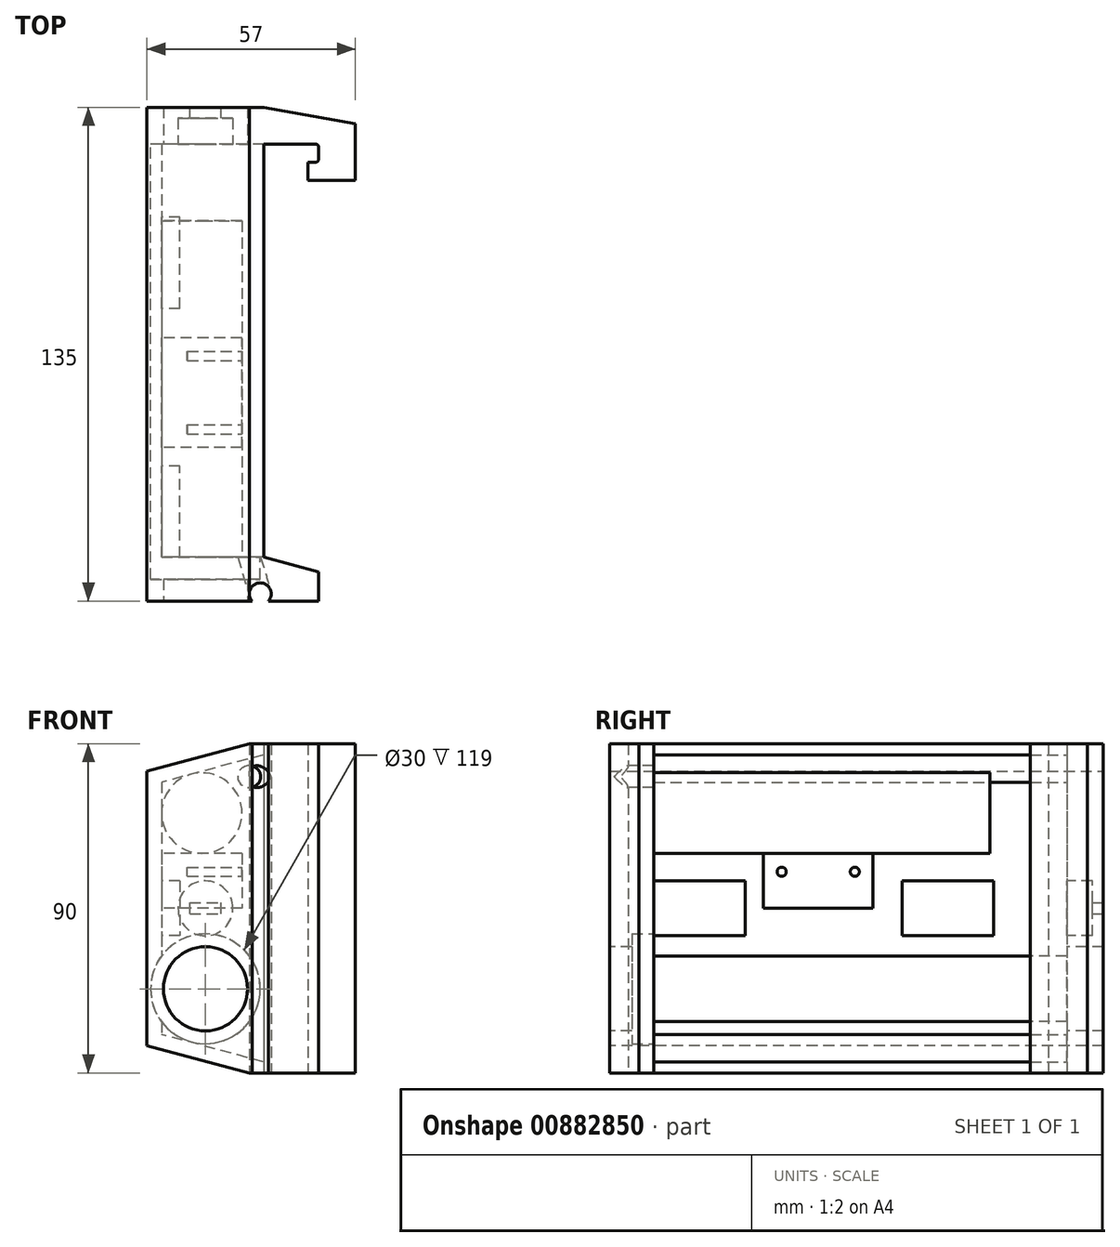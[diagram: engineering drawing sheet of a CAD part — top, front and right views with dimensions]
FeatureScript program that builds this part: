
annotation { "Feature Type Name" : "Feature", "Feature Type Description" : "" }
export const myFeature = defineFeature(function(context is Context, id is Id, definition is map)
    precondition{}
    {
        {
            var Q0;
            Q0=qCreatedBy(makeId("Top.planeOp"),FACE);
            var sketch = newSketch(context, id + "F0", { "sketchPlane" : qUnion([Q0])});
            skLineSegment(sketch, "E0", {"start": v(0, 0) * mm, "end": v(15, 0) * mm});
            skLineSegment(sketch, "E1", {"start": v(15, 0) * mm, "end": v(15, -5) * mm});
            skLineSegment(sketch, "E2", {"start": v(15, -5) * mm, "end": v(12, -5) * mm});
            skLineSegment(sketch, "E3", {"start": v(12, -5) * mm, "end": v(12, -10) * mm});
            skLineSegment(sketch, "E4", {"start": v(12, -10) * mm, "end": v(25, -10) * mm});
            skLineSegment(sketch, "E5", {"start": v(25, -10) * mm, "end": v(25, 10) * mm});
            skLineSegment(sketch, "E6", {"start": v(25, 10) * mm, "end": v(-32, 10) * mm});
            skLineSegment(sketch, "E7", {"start": v(-32, 10) * mm, "end": v(-32, -125) * mm});
            skLineSegment(sketch, "E8", {"start": v(15, -117.02) * mm, "end": v(0, -113) * mm});
            skLineSegment(sketch, "E9", {"start": v(0, -113) * mm, "end": v(0, 0) * mm});
            skLineSegment(sketch, "E10", {"start": v(-32, -125) * mm, "end": v(-3.24, -125) * mm});
            skLineSegment(sketch, "E11", {"start": v(15, -125) * mm, "end": v(15, -117.02) * mm});
            skArc(sketch, "E12", {"start": v(1.24, -125) * mm, "mid": v(-1, -120) * mm, "end": v(-3.24, -125) * mm});
            skLineSegment(sketch, "E13.trimOffspring", {"start": v(1.24, -125) * mm, "end": v(15, -125) * mm});
            skSolve(sketch);
        }
        {
            var Q0;
            Q0=qSketchRegion(id+"F0",true);
            extrude(context, id + "F1", {"entities" : qUnion([Q0]), "depth" : 90 * mm, "symmetric" : true});
        }
        {
            var Q0;
            Q0=makeQuery(id+"F1.opExtrude","CAP_EDGE",EDGE,{"disambiguationData":[OSD([sQuery(id+"F0.wireOp",EDGE,"E7")])],"isStart":false});
            chamfer(context, id + "F2", {"entities" : qUnion([Q0]), "chamferType" : ChamferType.OFFSET_ANGLE, "width" : 28 * mm, "oppositeDirection" : false, "angle" : 15 * degree, "tangentPropagation" : true});
        }
        {
            var Q0;
            Q0=makeQuery(id+"F1.opExtrude","CAP_EDGE",EDGE,{"disambiguationData":[OSD([sQuery(id+"F0.wireOp",EDGE,"E7")])],"isStart":true});
            chamfer(context, id + "F3", {"entities" : qUnion([Q0]), "chamferType" : ChamferType.OFFSET_ANGLE, "width" : 28 * mm, "oppositeDirection" : true, "angle" : 15 * degree, "tangentPropagation" : true});
        }
        {
            var Q0;
            Q0=makeQuery(id+"F1.opExtrude","SWEPT_FACE",FACE,{"disambiguationData":[OSD([sQuery(id+"F0.wireOp",EDGE,"E0")])]});
            var sketch = newSketch(context, id + "F4", { "sketchPlane" : qUnion([Q0])});
            skLineSegment(sketch, "E14", {"start": v(0, 0) * mm, "end": v(0, -42) * mm});
            skLineSegment(sketch, "E15", {"start": v(0, -42) * mm, "end": v(-28, -34.5) * mm});
            skLineSegment(sketch, "E16", {"start": v(-28, -34.5) * mm, "end": v(-28, 0) * mm});
            skLineSegment(sketch, "E17", {"start": v(-28, 0) * mm, "end": v(0, 0) * mm, "construction": true});
            skLineSegment(sketch, "E18.MirrorCS", {"start": v(0, 42) * mm, "end": v(-28, 34.5) * mm});
            skLineSegment(sketch, "E19.MirrorCS", {"start": v(0, 0) * mm, "end": v(0, 42) * mm});
            skLineSegment(sketch, "E20.MirrorCS", {"start": v(-28, 34.5) * mm, "end": v(-28, 0) * mm});
            skSolve(sketch);
        }
        {
            var Q0;
            Q0 = qSketchRegion(id + "F4", true);
            extrude(context, id + "F5", {"entities" : qUnion([Q0]), "operationType" : NewBodyOperationType.REMOVE, "depth" : 113 * mm, "offsetDistance" : 25 * mm});
        }
        {
            var Q0;
            Q0=makeQuery(id+"F1.opExtrude","SWEPT_FACE",FACE,{"disambiguationData":[OSD([sQuery(id+"F0.wireOp",EDGE,"E10")])]});
            var sketch = newSketch(context, id + "F6", { "sketchPlane" : qUnion([Q0])});
            skCircle(sketch, "E21", {"center": v(-16, -22) * mm, "radius": 11.5 * mm});
            skSolve(sketch);
        }
        {
            var Q0;
            Q0 = qSketchRegion(id + "F6", true);
            extrude(context, id + "F7", {"entities" : qUnion([Q0]), "operationType" : NewBodyOperationType.REMOVE, "endBound" : BoundingType.THROUGH_ALL, "oppositeDirection" : true, "depth" : 25 * mm, "offsetDistance" : 25 * mm});
        }
        {
            var Q0;
            Q0=makeQuery(id+"F5.boolean.opBoolean","COPY",FACE,{"derivedFrom":makeQuery(id+"F5.opExtrude","CAP_FACE",FACE,{"disambiguationData":[OSD([sQuery(id+"F4.wireOp",EDGE,"E14"),sQuery(id+"F4.wireOp",EDGE,"E15"),sQuery(id+"F4.wireOp",EDGE,"E16"),sQuery(id+"F4.wireOp",EDGE,"E19.MirrorCS"),sQuery(id+"F4.wireOp",EDGE,"E18.MirrorCS"),sQuery(id+"F4.wireOp",EDGE,"E20.MirrorCS")])],"isStart":false})});
            var sketch = newSketch(context, id + "F8", { "sketchPlane" : qUnion([Q0])});
            skCircle(sketch, "E22", {"center": v(16, -22) * mm, "radius": 15 * mm});
            skSolve(sketch);
        }
        {
            var Q0;
            Q0 = qSketchRegion(id + "F8", true);
            extrude(context, id + "F9", {"entities" : qUnion([Q0]), "operationType" : NewBodyOperationType.REMOVE, "oppositeDirection" : true, "depth" : 6 * mm, "offsetDistance" : 25 * mm});
        }
        {
            var Q0;
            Q0 = qSketchRegion(id + "F8", true);
            var Q1;
            Q1=makeQuery(id+"FtUT5HdTIuJWpzB_1.boolean.opBoolean","MERGE",FACE,{"derivedFrom":[makeQuery(id+"F1.opExtrude","SWEPT_FACE",FACE,{"disambiguationData":[OSD([sQuery(id+"F0.wireOp",EDGE,"E0")])]})],"fromTools":[makeQuery(id+"FtUT5HdTIuJWpzB_1.opExtrude","SWEPT_FACE",FACE,{"disambiguationData":[OSD([sQuery(id+"FxggytiENuwNWFf_1.wireOp",EDGE,"w0qHnqGK-W6aV-OTm7-zip8-LkYYj01r2KTm.left")])]})]});
            extrude(context, id + "F10", {"entities" : qUnion([Q0]), "operationType" : NewBodyOperationType.REMOVE, "endBound" : BoundingType.UP_TO_SURFACE, "depth" : 60 * mm, "endBoundEntityFace" : qUnion([Q1]), "offsetDistance" : 25 * mm});
        }
        {
            var Q0;
            {var subQ1=sQuery(id+"F4.wireOp",EDGE,"E20.MirrorCS");var subQ2=sQuery(id+"F4.wireOp",EDGE,"E18.MirrorCS");var subQ3=sQuery(id+"F4.wireOp",EDGE,"E16");Q0=makeQuery(id+"F10.boolean.opBoolean","SPLIT",FACE,{"disambiguationData":[TD([makeQuery(id+"F5.boolean.opBoolean","COPY",FACE,{"derivedFrom":makeQuery(id+"F5.opExtrude","SWEPT_FACE",FACE,{"disambiguationData":[OSD([subQ2])]})})])],"derivedFrom":makeQuery(id+"F5.boolean.opBoolean","COPY",FACE,{"derivedFrom":makeQuery(id+"F5.opExtrude","SWEPT_FACE",FACE,{"disambiguationData":[OSD([subQ3,subQ1])]})})});}
            var sketch = newSketch(context, id + "F11", { "sketchPlane" : qUnion([Q0])});
            skLineSegment(sketch, "E23.bottom", {"start": v(-83, 15) * mm, "end": v(-53, 15) * mm});
            skLineSegment(sketch, "E23.top", {"start": v(-83, 0) * mm, "end": v(-53, 0) * mm});
            skLineSegment(sketch, "E23.left", {"start": v(-83, 15) * mm, "end": v(-83, 0) * mm});
            skLineSegment(sketch, "E23.right", {"start": v(-53, 15) * mm, "end": v(-53, 0) * mm});
            skSolve(sketch);
        }
        {
            var Q0;
            Q0 = qSketchRegion(id + "F11", true);
            extrude(context, id + "F12", {"entities" : qUnion([Q0]), "operationType" : NewBodyOperationType.ADD, "depth" : 22 * mm, "offsetDistance" : 25 * mm});
        }
        {
            var Q0;
            Q0=makeQuery(id+"F12.opExtrude","CAP_FACE",FACE,{"disambiguationData":[OSD([sQuery(id+"F11.wireOp",EDGE,"E23.bottom"),sQuery(id+"F11.wireOp",EDGE,"E23.top"),sQuery(id+"F11.wireOp",EDGE,"E23.left"),sQuery(id+"F11.wireOp",EDGE,"E23.right")])],"isStart":false});
            var sketch = newSketch(context, id + "F13", { "sketchPlane" : qUnion([Q0])});
            skCircle(sketch, "E24", {"center": v(-78, 10) * mm, "radius": 1.25 * mm});
            skCircle(sketch, "E25", {"center": v(-58, 10) * mm, "radius": 1.25 * mm});
            skLineSegment(sketch, "E26", {"start": v(-78, 10) * mm, "end": v(-58, 10) * mm, "construction": true});
            skLineSegment(sketch, "E27", {"start": v(-68, 10) * mm, "end": v(-68, 15) * mm, "construction": true});
            skSolve(sketch);
        }
        {
            var Q0;
            Q0 = qSketchRegion(id + "F13", true);
            extrude(context, id + "F14", {"entities" : qUnion([Q0]), "operationType" : NewBodyOperationType.REMOVE, "oppositeDirection" : true, "depth" : 15 * mm, "offsetDistance" : 25 * mm});
        }
        {
            var Q0;
            Q0=makeQuery(id+"F1.opExtrude","SWEPT_FACE",FACE,{"disambiguationData":[OSD([sQuery(id+"F0.wireOp",EDGE,"E6")])]});
            var sketch = newSketch(context, id + "F15", { "sketchPlane" : qUnion([Q0])});
            skLineSegment(sketch, "E28.bottom", {"start": v(20.25, -1.5) * mm, "end": v(11.75, -1.5) * mm});
            skLineSegment(sketch, "E28.top", {"start": v(20.25, 1.5) * mm, "end": v(11.75, 1.5) * mm});
            skLineSegment(sketch, "E28.left", {"start": v(20.25, -1.5) * mm, "end": v(20.25, 1.5) * mm});
            skLineSegment(sketch, "E28.right", {"start": v(11.75, -1.5) * mm, "end": v(11.75, 1.5) * mm});
            skLineSegment(sketch, "E29", {"start": v(16, -22) * mm, "end": v(16, -1.5) * mm, "construction": true});
            skLineSegment(sketch, "E30", {"start": v(11.75, 0) * mm, "end": v(0, 0) * mm, "construction": true});
            skSolve(sketch);
        }
        {
            var Q0;
            Q0 = qSketchRegion(id + "F15", true);
            extrude(context, id + "F16", {"entities" : qUnion([Q0]), "operationType" : NewBodyOperationType.REMOVE, "endBound" : BoundingType.UP_TO_NEXT, "oppositeDirection" : true, "depth" : 25 * mm, "offsetDistance" : 25 * mm});
        }
        {
            var Q0;
            Q0=makeQuery(id+"F10.boolean.opBoolean","MERGE",FACE,{"derivedFrom":[makeQuery(id+"F5.boolean.opBoolean","MERGE",FACE,{"derivedFrom":[makeQuery(id+"F1.opExtrude","SWEPT_FACE",FACE,{"disambiguationData":[OSD([sQuery(id+"F0.wireOp",EDGE,"E0")])]})],"fromTools":[makeQuery(id+"F5.opExtrude","CAP_FACE",FACE,{"disambiguationData":[OSD([sQuery(id+"F4.wireOp",EDGE,"E14"),sQuery(id+"F4.wireOp",EDGE,"E15"),sQuery(id+"F4.wireOp",EDGE,"E16"),sQuery(id+"F4.wireOp",EDGE,"E19.MirrorCS"),sQuery(id+"F4.wireOp",EDGE,"E18.MirrorCS"),sQuery(id+"F4.wireOp",EDGE,"E20.MirrorCS")])],"isStart":true})]})],"fromTools":[makeQuery(id+"F10.opExtrude","CAP_FACE",FACE,{"disambiguationData":[OSD([sQuery(id+"F8.wireOp",EDGE,"E22")])],"isStart":false})]});
            var sketch = newSketch(context, id + "F17", { "sketchPlane" : qUnion([Q0])});
            skLineSegment(sketch, "E31", {"start": v(-20.25, 1.5) * mm, "end": v(-11.75, -1.5) * mm, "construction": true});
            skCircle(sketch, "E32", {"center": v(-16, 0) * mm, "radius": 7.5 * mm});
            skSolve(sketch);
        }
        {
            var Q0;
            Q0 = qSketchRegion(id + "F17", true);
            extrude(context, id + "F18", {"entities" : qUnion([Q0]), "operationType" : NewBodyOperationType.REMOVE, "oppositeDirection" : true, "depth" : 7 * mm, "offsetDistance" : 25 * mm});
        }
        {
            var Q0;
            {var subQ1=sQuery(id+"F4.wireOp",EDGE,"E20.MirrorCS");var subQ2=sQuery(id+"F4.wireOp",EDGE,"E18.MirrorCS");var subQ3=sQuery(id+"F4.wireOp",EDGE,"E16");Q0=makeQuery(id+"F10.boolean.opBoolean","SPLIT",FACE,{"disambiguationData":[TD([makeQuery(id+"F5.boolean.opBoolean","COPY",FACE,{"derivedFrom":makeQuery(id+"F5.opExtrude","SWEPT_FACE",FACE,{"disambiguationData":[OSD([subQ2])]})})])],"derivedFrom":makeQuery(id+"F5.boolean.opBoolean","COPY",FACE,{"derivedFrom":makeQuery(id+"F5.opExtrude","SWEPT_FACE",FACE,{"disambiguationData":[OSD([subQ3,subQ1])]})})});}
            var sketch = newSketch(context, id + "F19", { "sketchPlane" : qUnion([Q0])});
            skPoint(sketch, "E33.firstSnap0", {"position": v(-83, 7.5) * mm});
            skLineSegment(sketch, "E33.bottom", {"start": v(-113, 7.5) * mm, "end": v(-88, 7.5) * mm});
            skLineSegment(sketch, "E33.top", {"start": v(-113, -7.5) * mm, "end": v(-88, -7.5) * mm});
            skLineSegment(sketch, "E33.left", {"start": v(-113, 7.5) * mm, "end": v(-113, -7.5) * mm});
            skLineSegment(sketch, "E33.right", {"start": v(-88, 7.5) * mm, "end": v(-88, -7.5) * mm});
            skLineSegment(sketch, "E34.bottom", {"start": v(-45, 7.5) * mm, "end": v(-20, 7.5) * mm});
            skLineSegment(sketch, "E34.top", {"start": v(-45, -7.5) * mm, "end": v(-20, -7.5) * mm});
            skLineSegment(sketch, "E34.left", {"start": v(-45, 7.5) * mm, "end": v(-45, -7.5) * mm});
            skLineSegment(sketch, "E34.right", {"start": v(-20, 7.5) * mm, "end": v(-20, -7.5) * mm});
            skLineSegment(sketch, "E35", {"start": v(13.82, 0) * mm, "end": v(-20, 0) * mm, "construction": true});
            skSolve(sketch);
        }
        {
            var Q0;
            Q0 = qSketchRegion(id + "F19", true);
            extrude(context, id + "F20", {"entities" : qUnion([Q0]), "operationType" : NewBodyOperationType.ADD, "depth" : 5 * mm, "offsetDistance" : 25 * mm});
        }
        {
            var Q0;
            Q0=makeQuery(id+"F1.opExtrude","SWEPT_EDGE",EDGE,{"disambiguationData":[OSD([sQuery(id+"F0.wireOp",EDGE,"E5"),sQuery(id+"F0.wireOp",EDGE,"E6")])]});
            chamfer(context, id + "F21", {"entities" : qUnion([Q0]), "chamferType" : ChamferType.OFFSET_ANGLE, "width" : 25 * mm, "oppositeDirection" : false, "angle" : 10 * degree, "tangentPropagation" : true});
        }
        {
            var Q0;
            Q0=qCreatedBy(makeId("Top.planeOp"),FACE);
            cPlane(context, id + "F22", {"entities" : qUnion([Q0]), "cplaneType" : CPlaneType.OFFSET, "offset" : 36 * mm, "width" : 150 * mm, "height" : 150 * mm});
        }
        {
            var Q0;
            Q0=qCreatedBy(id+"F22.planeOp",FACE);
            var sketch = newSketch(context, id + "F23", { "sketchPlane" : qUnion([Q0])});
            skLineSegment(sketch, "E36", {"start": v(-7.8, -100.65) * mm, "end": v(-1, -123) * mm});
            skLineSegment(sketch, "E37", {"start": v(-7.8, -100.65) * mm, "end": v(-4.93, -99.78) * mm});
            skLineSegment(sketch, "E38", {"start": v(-4.93, -99.78) * mm, "end": v(1.87, -122.13) * mm});
            skLineSegment(sketch, "E39", {"start": v(1.87, -122.13) * mm, "end": v(-1, -123) * mm});
            skSolve(sketch);
        }
        {
            var Q0;
            Q0 = qSketchRegion(id + "F23", true);
            var Q1;
            Q1=sQuery(id+"F23.wireOp",EDGE,"E36");
            revolve(context, id + "F24", {"operationType" : NewBodyOperationType.REMOVE, "surfaceOperationType" : NewSurfaceOperationType.NEW, "entities" : qUnion([Q0]), "axis" : qUnion([Q1]), "revolveType" : RevolveType.FULL, "oppositeDirection" : true});
        }
        {
            var Q0;
            Q0=makeQuery(id+"F5.boolean.opBoolean","COPY",FACE,{"derivedFrom":makeQuery(id+"F5.opExtrude","CAP_FACE",FACE,{"disambiguationData":[OSD([sQuery(id+"F4.wireOp",EDGE,"E14"),sQuery(id+"F4.wireOp",EDGE,"E15"),sQuery(id+"F4.wireOp",EDGE,"E16"),sQuery(id+"F4.wireOp",EDGE,"E19.MirrorCS"),sQuery(id+"F4.wireOp",EDGE,"E18.MirrorCS"),sQuery(id+"F4.wireOp",EDGE,"E20.MirrorCS")])],"isStart":false})});
            var sketch = newSketch(context, id + "F25", { "sketchPlane" : qUnion([Q0])});
            skCircle(sketch, "E40", {"center": v(17, 26.06) * mm, "radius": 11 * mm});
            skSolve(sketch);
        }
        {
            var Q0;
            Q0 = qSketchRegion(id + "F25", true);
            extrude(context, id + "F26", {"entities" : qUnion([Q0]), "depth" : 92 * mm, "offsetDistance" : 25 * mm});
        }
        {
            var Q0;
            Q0=makeQuery(id+"F1.opExtrude","SWEPT_EDGE",EDGE,{"disambiguationData":[OSD([sQuery(id+"F0.wireOp",EDGE,"E0"),sQuery(id+"F0.wireOp",EDGE,"E1")])]});
            var Q1;
            Q1=makeQuery(id+"F1.opExtrude","SWEPT_EDGE",EDGE,{"disambiguationData":[OSD([sQuery(id+"F0.wireOp",EDGE,"E1"),sQuery(id+"F0.wireOp",EDGE,"E2")])]});
            fillet(context, id + "F27", {"entities" : qUnion([Q0, Q1]), "radius" : 1 * mm, "tangentPropagation" : true, "allowEdgeOverflow" : false});
        }
    });
